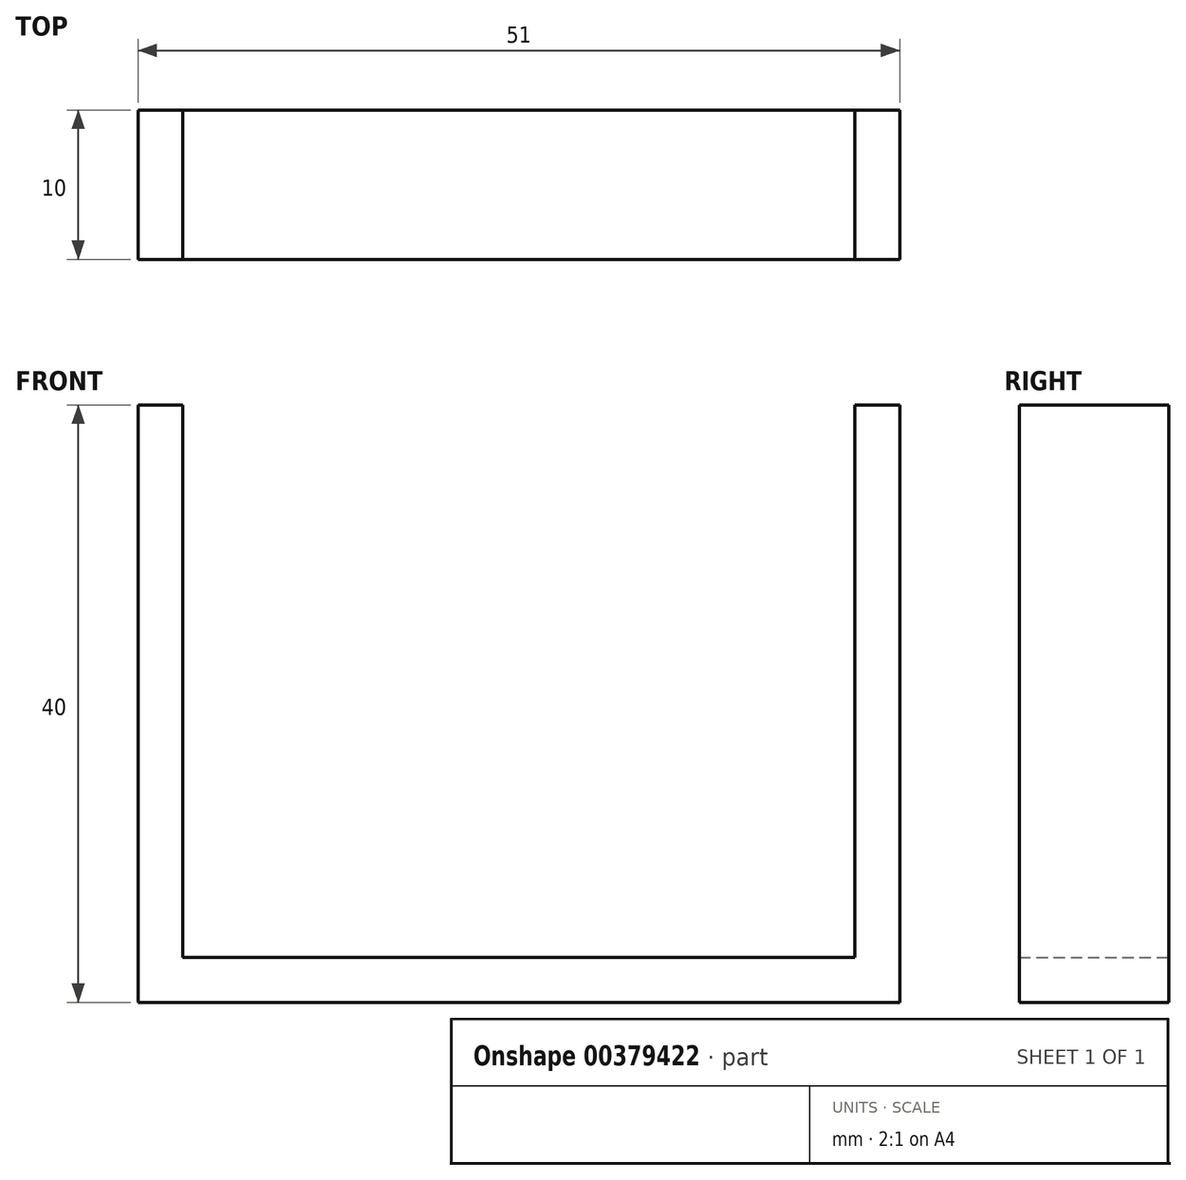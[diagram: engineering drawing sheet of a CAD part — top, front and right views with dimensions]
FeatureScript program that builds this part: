
annotation { "Feature Type Name" : "Feature", "Feature Type Description" : "" }
export const myFeature = defineFeature(function(context is Context, id is Id, definition is map)
    precondition{}
    {
        {
            var Q0;
            Q0=qCreatedBy(makeId("Front.planeOp"),FACE);
            var sketch = newSketch(context, id + "F0", { "sketchPlane" : qUnion([Q0])});
            skLineSegment(sketch, "E0", {"start": v(0, 0) * mm, "end": v(22.5, 0) * mm, "construction": true});
            skLineSegment(sketch, "E1", {"start": v(22.5, 0) * mm, "end": v(25.5, 0) * mm});
            skLineSegment(sketch, "E2", {"start": v(25.5, 0) * mm, "end": v(25.5, -5) * mm});
            skLineSegment(sketch, "E3", {"start": v(25.5, -5) * mm, "end": v(25.5, -40) * mm});
            skLineSegment(sketch, "E4", {"start": v(25.5, -40) * mm, "end": v(0, -40) * mm});
            skLineSegment(sketch, "E5", {"start": v(22.5, 0) * mm, "end": v(22.5, -37) * mm});
            skLineSegment(sketch, "E6", {"start": v(22.5, -37) * mm, "end": v(0, -37) * mm});
            skLineSegment(sketch, "E7", {"start": v(0, -37) * mm, "end": v(0, 0) * mm, "construction": true});
            skLineSegment(sketch, "E8.MirrorCS", {"start": v(-22.5, 0) * mm, "end": v(-25.5, 0) * mm});
            skLineSegment(sketch, "E9.MirrorCS", {"start": v(-25.5, 0) * mm, "end": v(-25.5, -5) * mm});
            skLineSegment(sketch, "E10.MirrorCS", {"start": v(0, 0) * mm, "end": v(-22.5, 0) * mm, "construction": true});
            skLineSegment(sketch, "E11.MirrorCS", {"start": v(-22.5, -37) * mm, "end": v(0, -37) * mm});
            skLineSegment(sketch, "E12.MirrorCS", {"start": v(-25.5, -5) * mm, "end": v(-25.5, -40) * mm});
            skLineSegment(sketch, "E13.MirrorCS", {"start": v(-25.5, -40) * mm, "end": v(0, -40) * mm});
            skLineSegment(sketch, "E14.MirrorCS", {"start": v(-22.5, 0) * mm, "end": v(-22.5, -37) * mm});
            skSolve(sketch);
        }
        {
            var Q0;
            Q0 = qSketchRegion(id + "F0", true);
            extrude(context, id + "F1", {"entities" : qUnion([Q0]), "depth" : 10 * mm});
        }
    });
